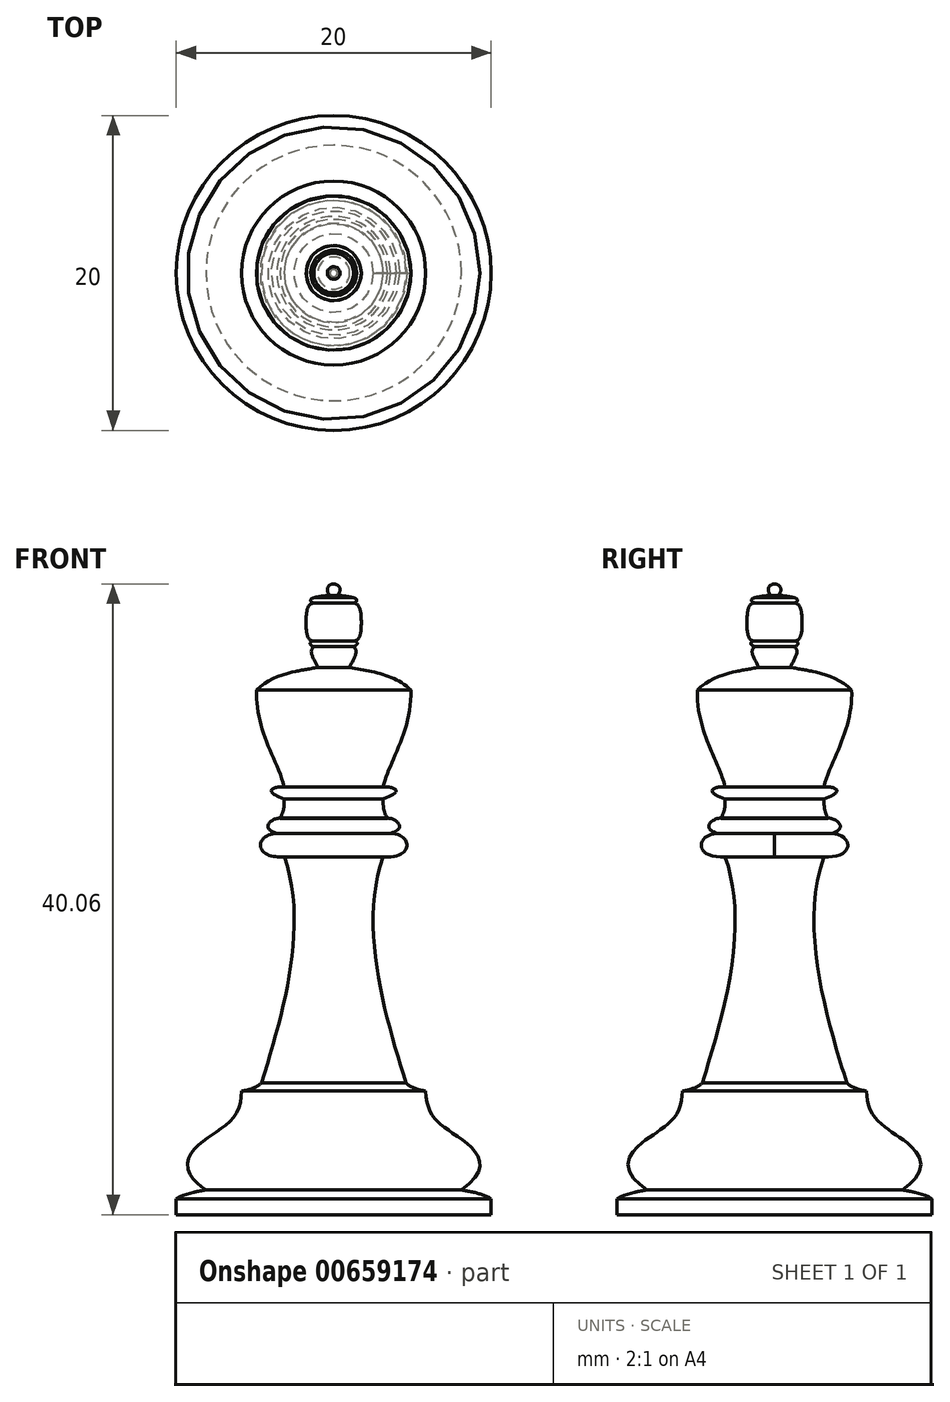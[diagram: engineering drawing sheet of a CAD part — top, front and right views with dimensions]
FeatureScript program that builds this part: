
annotation { "Feature Type Name" : "Feature", "Feature Type Description" : "" }
export const myFeature = defineFeature(function(context is Context, id is Id, definition is map)
    precondition{}
    {
        {
            var Q0;
            Q0=qCreatedBy(makeId("Front.planeOp"),FACE);
            var sketch = newSketch(context, id + "F0", { "sketchPlane" : qUnion([Q0])});
            skLineSegment(sketch, "E0", {"start": v(0, 0) * mm, "end": v(-10, 0) * mm});
            skLineSegment(sketch, "E1", {"start": v(-10, 0) * mm, "end": v(-10, 1) * mm});
            skFitSpline(sketch, "E2", {"points": [v(-10, 1) * mm, v(-8.12, 1.57) * mm], "startDerivative": vector(1.65, 1.05) * mm, "endDerivative": vector(1.97, 0.35) * mm});
            skFitSpline(sketch, "E3", {"points": [v(-8.12, 1.57) * mm, v(-7.6, 5.14) * mm, v(-5.84, 7.85) * mm], "startDerivative": vector(-13.77, 9.65) * mm, "endDerivative": vector(0.4, 9.34) * mm});
            skFitSpline(sketch, "E4", {"points": [v(-5.84, 7.85) * mm, v(-4.59, 8.36) * mm], "startDerivative": vector(1.42, 0.22) * mm, "endDerivative": vector(1.08, 0.93) * mm});
            skFitSpline(sketch, "E5", {"points": [v(-4.59, 8.36) * mm, v(-3.14, 22.74) * mm], "startDerivative": vector(3.79, 12.32) * mm, "endDerivative": vector(-4.83, 13.57) * mm});
            skFitSpline(sketch, "E6", {"points": [v(-3.14, 22.74) * mm, v(-3.6, 24.22) * mm], "startDerivative": vector(-5.89, -0.54) * mm, "endDerivative": vector(4.32, 0.1) * mm});
            skFitSpline(sketch, "E7", {"points": [v(-3.6, 24.22) * mm, v(-3.4, 25.18) * mm], "startDerivative": vector(-3.6, 1.07) * mm, "endDerivative": vector(1.24, -0.21) * mm});
            skFitSpline(sketch, "E8", {"points": [v(-3.4, 25.18) * mm, v(-3.14, 26.4) * mm], "startDerivative": vector(0.76, 1.24) * mm, "endDerivative": vector(-0.02, 1.25) * mm});
            skFitSpline(sketch, "E9", {"points": [v(-3.14, 26.4) * mm, v(-3.14, 27.17) * mm], "startDerivative": vector(-5.06, 1.83) * mm, "endDerivative": vector(0.94, -0.17) * mm});
            skFitSpline(sketch, "E10", {"points": [v(-3.14, 27.17) * mm, v(-4.9, 33.33) * mm], "startDerivative": vector(-0.96, 4.6) * mm, "endDerivative": vector(0.31, 7.8) * mm});
            skFitSpline(sketch, "E11", {"points": [v(-4.9, 33.33) * mm, v(-1.02, 34.76) * mm], "startDerivative": vector(3.2, 3.06) * mm, "endDerivative": vector(3.87, 0.66) * mm});
            skFitSpline(sketch, "E12", {"points": [v(-1.02, 34.76) * mm, v(-1.26, 36.08) * mm], "startDerivative": vector(-0.71, 1.74) * mm, "endDerivative": vector(1.18, 0.9) * mm});
            skFitSpline(sketch, "E13", {"points": [v(-1.26, 36.08) * mm, v(-1.26, 36.45) * mm], "startDerivative": vector(-0.82, 0.28) * mm, "endDerivative": vector(1.1, 0.24) * mm});
            skFitSpline(sketch, "E14", {"points": [v(-1.26, 36.45) * mm, v(-1.75, 37.61) * mm], "startDerivative": vector(-1.2, -0.08) * mm, "endDerivative": vector(0, 2.17) * mm});
            skFitSpline(sketch, "E15", {"points": [v(-1.75, 37.61) * mm, v(-1.26, 38.85) * mm], "startDerivative": vector(0, 2.17) * mm, "endDerivative": vector(1.2, 0.01) * mm});
            skFitSpline(sketch, "E16", {"points": [v(-1.26, 38.85) * mm, v(-1.26, 39.19) * mm], "startDerivative": vector(-0.97, 0.28) * mm, "endDerivative": vector(0.62, 0.05) * mm});
            skFitSpline(sketch, "E17", {"points": [v(-1.26, 39.19) * mm, v(-0.23, 39.33) * mm], "startDerivative": vector(0.97, 0.26) * mm, "endDerivative": vector(1.1, 0.07) * mm});
            skFitSpline(sketch, "E18", {"points": [v(-0.23, 39.33) * mm, v(0, 40.06) * mm], "startDerivative": vector(-1.07, 1.15) * mm, "endDerivative": vector(0.96, -0.05) * mm});
            skLineSegment(sketch, "E19", {"start": v(0, 40.06) * mm, "end": v(0, 0) * mm});
            skSolve(sketch);
        }
        {
            var Q0;
            Q0 = qSketchRegion(id + "F0", true);
            var Q1;
            Q1=sQuery(id+"F0.wireOp",EDGE,"E19");
            revolve(context, id + "F1", {"entities" : qUnion([Q0]), "axis" : qUnion([Q1]), "revolveType" : RevolveType.FULL});
        }
    });
